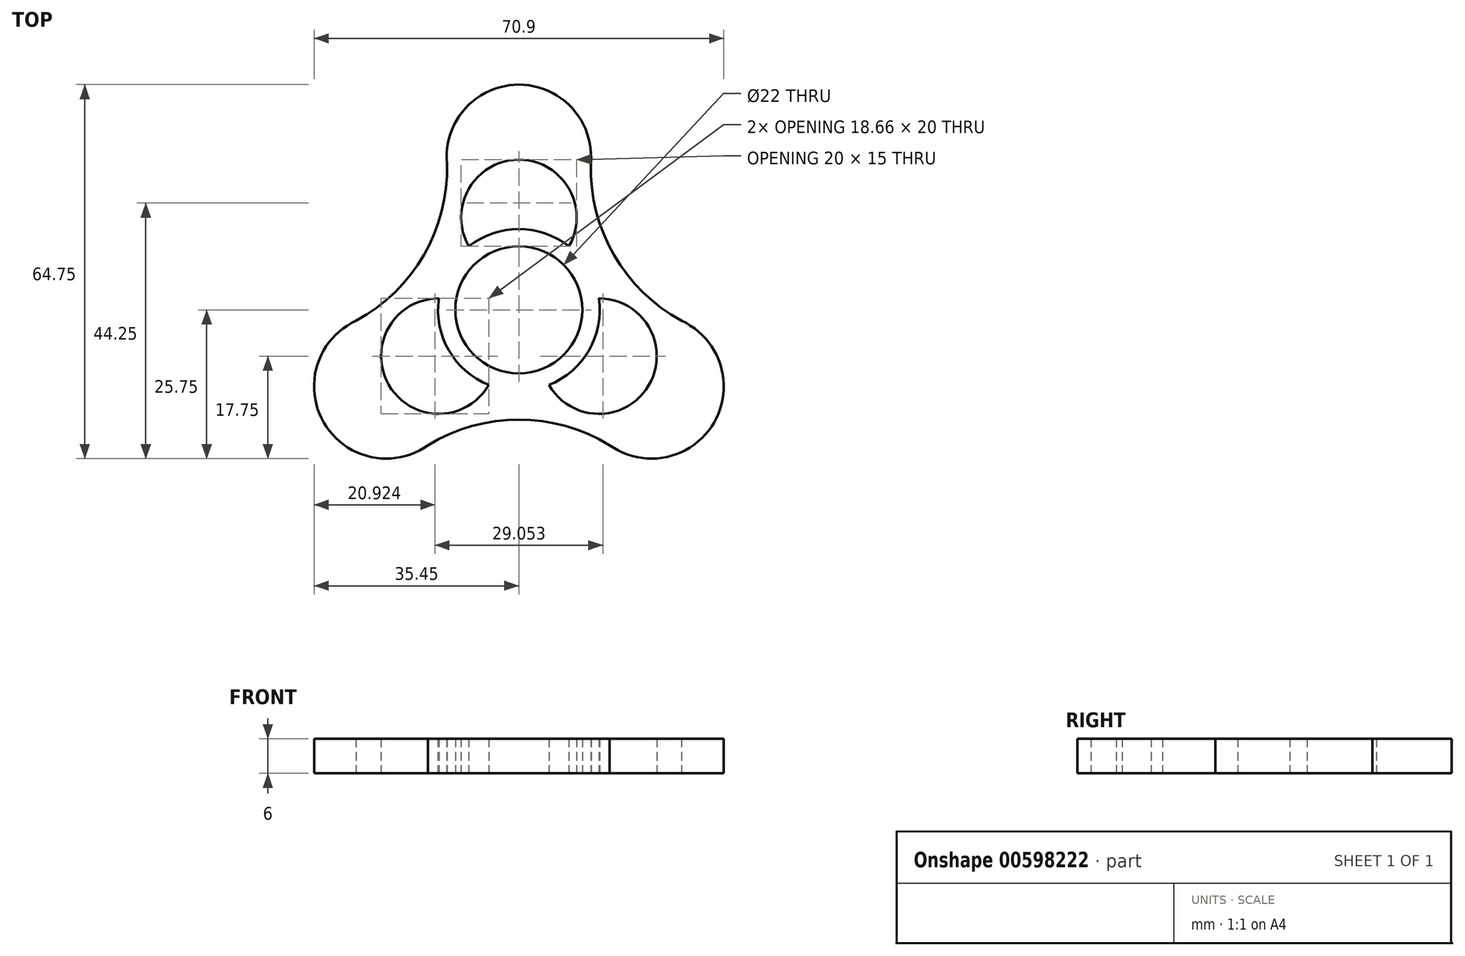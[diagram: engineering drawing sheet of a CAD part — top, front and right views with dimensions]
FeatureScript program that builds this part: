
annotation { "Feature Type Name" : "Feature", "Feature Type Description" : "" }
export const myFeature = defineFeature(function(context is Context, id is Id, definition is map)
    precondition{}
    {
        {
            var Q0;
            Q0=qCreatedBy(makeId("Top.planeOp"),FACE);
            var sketch = newSketch(context, id + "F0", { "sketchPlane" : qUnion([Q0])});
            skArc(sketch, "E0", {"start": v(-6.79, 8.66) * mm, "mid": v(-9.53, 5.5) * mm, "end": v(-10.9, 1.55) * mm});
            skLineSegment(sketch, "E1", {"start": v(0, 26.5) * mm, "end": v(0, 0) * mm, "construction": true});
            skLineSegment(sketch, "E2", {"start": v(0, 0) * mm, "end": v(-22.95, -13.25) * mm, "construction": true});
            skLineSegment(sketch, "E3", {"start": v(0, 0) * mm, "end": v(22.95, -13.25) * mm, "construction": true});
            skArc(sketch, "E4", {"start": v(12.44, 25.32) * mm, "mid": v(0, 39) * mm, "end": v(-12.44, 25.32) * mm});
            skArc(sketch, "E5", {"start": v(15.7, -23.44) * mm, "mid": v(33.77, -19.5) * mm, "end": v(28.15, -1.88) * mm});
            skArc(sketch, "E6", {"start": v(-28.15, -1.88) * mm, "mid": v(-33.77, -19.5) * mm, "end": v(-15.7, -23.44) * mm});
            skLineSegment(sketch, "E7", {"start": v(22.95, -13.25) * mm, "end": v(29.2, -2.42) * mm, "construction": true});
            skArc(sketch, "E8", {"start": v(12.44, 25.32) * mm, "mid": v(16.45, 9.5) * mm, "end": v(28.15, -1.88) * mm});
            skArc(sketch, "E9.MirrorCS", {"start": v(-12.44, 25.32) * mm, "mid": v(-16.45, 9.5) * mm, "end": v(-28.15, -1.88) * mm});
            skArc(sketch, "E10.MirrorCS", {"start": v(-15.7, -23.44) * mm, "mid": v(0, -19) * mm, "end": v(15.7, -23.44) * mm});
            skArc(sketch, "E11", {"start": v(8.66, 11) * mm, "mid": v(0, 26) * mm, "end": v(-8.66, 11) * mm});
            skArc(sketch, "E12.MirrorC", {"start": v(13.86, 2) * mm, "mid": v(22.52, -13) * mm, "end": v(5.2, -13) * mm});
            skArc(sketch, "E13.MirrorC", {"start": v(-5.2, -13) * mm, "mid": v(-22.52, -13) * mm, "end": v(-13.86, 2) * mm});
            skArc(sketch, "E14.trimOffspring", {"start": v(10.9, 1.55) * mm, "mid": v(9.53, 5.5) * mm, "end": v(6.79, 8.66) * mm});
            skArc(sketch, "E15.trimOffspring", {"start": v(-4.1, -10.2) * mm, "mid": v(0, -11) * mm, "end": v(4.1, -10.2) * mm});
            skPoint(sketch, "E16.orphan", {"position": v(16.7, -24.08) * mm});
            skPoint(sketch, "E17.orphan", {"position": v(-16.7, -24.08) * mm});
            skPoint(sketch, "E18.orphan", {"position": v(-29.2, -2.42) * mm});
            skPoint(sketch, "E19.orphan", {"position": v(-12.5, 26.5) * mm});
            skPoint(sketch, "E20.orphan", {"position": v(12.5, 26.5) * mm});
            skArc(sketch, "E21", {"start": v(-13.86, 2) * mm, "mid": v(-12.12, -7) * mm, "end": v(-5.2, -13) * mm});
            skArc(sketch, "E22.trimOffspring", {"start": v(5.2, -13) * mm, "mid": v(12.12, -7) * mm, "end": v(13.86, 2) * mm});
            skArc(sketch, "E23.trimOffspring", {"start": v(8.66, 11) * mm, "mid": v(0, 14) * mm, "end": v(-8.66, 11) * mm});
            skCircle(sketch, "E24", {"center": v(0, 0) * mm, "radius": 11 * mm});
            skSolve(sketch);
        }
        {
            var Q0;
            Q0=makeQuery(id+"F0.imprint","IMPRINT",FACE,{"disambiguationData":[TD([[makeQuery(id+"F0.imprint","IMPRINT",EDGE,{"derivedFrom":sQuery(id+"F0.wireOp",EDGE,"E4")}),1.0]])]});
            extrude(context, id + "F1", {"entities" : qUnion([Q0]), "depth" : 6 * mm, "offsetDistance" : 25 * mm});
        }
        {
            var Q0;
            Q0=qCreatedBy(makeId("Top.planeOp"),FACE);
            var sketch = newSketch(context, id + "F2", { "sketchPlane" : qUnion([Q0])});
            skCircle(sketch, "E25", {"center": v(0, 0) * mm, "radius": 11 * mm});
            skSolve(sketch);
        }
        {
            var Q0;
            Q0=makeQuery(id+"F2.imprint","IMPRINT",FACE,{"disambiguationData":[TD([[makeQuery(id+"F2.imprint","IMPRINT",EDGE,{"derivedFrom":sQuery(id+"F2.wireOp",EDGE,"E25")}),1.0]])]});
            extrude(context, id + "F3", {"entities" : qUnion([Q0]), "depth" : 6 * mm, "offsetDistance" : 25 * mm});
        }
    });
